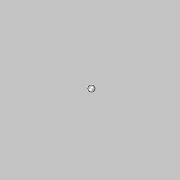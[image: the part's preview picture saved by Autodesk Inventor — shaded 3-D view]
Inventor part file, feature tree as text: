
AUTODESK INVENTOR PART (.ipt)
format: ipt  version: 2017 (Build 210142000, 142)  size: 199,680 bytes
history: native  units: mm
features: sketch x14, extrude x11, mirror x2, chamfer x1, sweep x1, hole x1
ambient origin geometry x8: Origin, YZ Plane, XZ Plane, XY Plane, X Axis, Y Axis, Z Axis, Center Point
bodies: Solid1 (feature_tree)
feature tree (30):
  extrude  "Extrusion1"  Depth=126.0mm
  extrude  "Extrusion2"  Depth=76.0mm
  extrude  "Extrusion3"  Depth=5.0mm
  extrude  "Extrusion4"  Depth=102.0mm
  extrude  "Extrusion5"  Depth=132.0mm TaperAngle=0.0deg
  extrude  "Extrusion6"  Depth=78.0mm
  extrude  "Extrusion7"  Depth=56.0mm
  mirror  "Mirror1"
  chamfer  "Chamfer1"  Distance=30.0mm
  extrude  "Extrusion8"  Depth=77.0mm
  extrude  "Extrusion9"  Depth=30.0mm TaperAngle=0.0deg
  extrude  "Extrusion10"  Depth=45.0mm
  sweep  "Sweep1"
  mirror  "Mirror2"
  hole  "Hole1"  [1 undecoded]
  extrude  "Extrusion11"  Depth=8.0mm
  sketch  "Sketch1"  dims[d0=104.0mm d1=126.0mm]
  sketch  "Sketch2"  dims[d2=80.0mm d3=0.0mm d5=76.0mm]
  sketch  "Sketch3"  dims[d6=180.0mm d7=5.0mm]
  sketch  "Sketch4"  dims[d8=50.0mm d9=102.0mm]
  sketch  "Sketch5"  dims[d10=196.0mm d11=132.0mm d12=0.0mm]
  sketch  "Sketch6"  dims[d13=131.6mm d14=78.0mm]
  sketch  "Sketch7"  dims[d15=12.0mm d16=0.0mm d17=56.0mm d18=30.0mm d19=0.0mm]
  sketch  "Sketch8"  dims[d21=30.0mm d22=0.0mm d23=77.0mm]
  sketch  "Sketch9"  dims[d24=30.0mm d25=0.0mm d28=30.0mm d29=0.0mm]
  sketch  "Sketch10"  dims[d30=25.0mm d31=2.0mm d32=45.0deg d33=45.0mm]
  sketch  "3D Sketch1"
  sketch  "Sketch11"  dims[d35=12.0mm d36=0.0mm d37=56.0mm]
  sketch  "Sketch12"  dims[d38=30.0mm d40=15.0mm]
  sketch  "Sketch13"  dims[d41=3.0mm d42=0.0mm d43=8.0mm d44=80.0mm d45=17.0mm d46=25.0mm d47=0.0mm d48=104.0mm d49=91.0mm d50=81.0mm d51=25.0mm d52=25.0mm d53=15.0mm d54=12.990381mm d55=0.0mm d56=0.0mm d57=147.7mm d58=50.8mm d59=154.0mm d60=6.0mm d61=6.0mm d62=4.0mm d63=2.0mm d64=90.0deg d65=8.0mm d66=20.594885mm d67=12.0mm d68=50.0mm d69=0.0mm d70=0.0mm]
note: 1 required parameter value undecoded (feature->parameter linkage not recoverable at this tier; creation-order binding heuristic only, values carry confidence <= 0.55)
